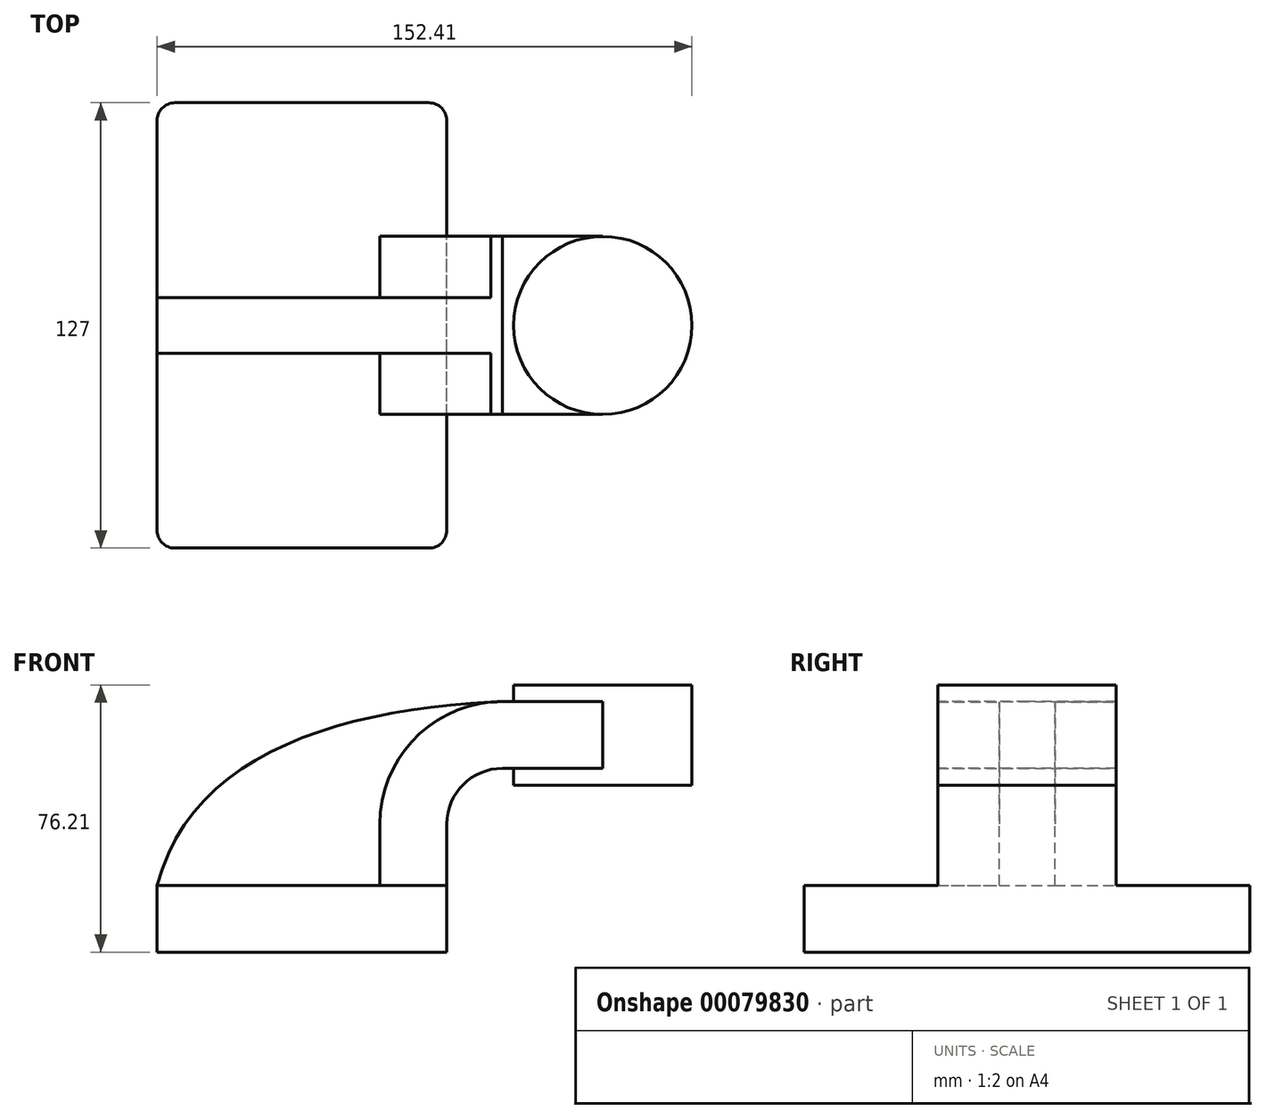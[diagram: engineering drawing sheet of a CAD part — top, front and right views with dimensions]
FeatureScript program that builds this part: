
annotation { "Feature Type Name" : "Feature", "Feature Type Description" : "" }
export const myFeature = defineFeature(function(context is Context, id is Id, definition is map)
    precondition{}
    {
        {
            var Q0;
            Q0=qCreatedBy(makeId("Front.planeOp"),FACE);
            var sketch = newSketch(context, id + "F0", { "sketchPlane" : qUnion([Q0])});
            skLineSegment(sketch, "E0.bottom", {"start": v(-41.28, 9.52) * mm, "end": v(41.28, 9.53) * mm});
            skLineSegment(sketch, "E0.top", {"start": v(-41.28, -9.53) * mm, "end": v(41.28, -9.53) * mm});
            skLineSegment(sketch, "E0.left", {"start": v(-41.28, 9.52) * mm, "end": v(-41.28, -9.53) * mm});
            skLineSegment(sketch, "E0.right", {"start": v(41.28, 9.53) * mm, "end": v(41.28, -9.52) * mm});
            skPoint(sketch, "E0.middle", {"position": v(0, 0) * mm});
            skLineSegment(sketch, "E1.bottom", {"start": v(60.33, 38.1) * mm, "end": v(111.13, 38.1) * mm});
            skLineSegment(sketch, "E1.top", {"start": v(60.32, 66.68) * mm, "end": v(111.12, 66.68) * mm});
            skLineSegment(sketch, "E1.left", {"start": v(60.33, 38.1) * mm, "end": v(60.32, 66.68) * mm});
            skLineSegment(sketch, "E1.right", {"start": v(111.13, 38.1) * mm, "end": v(111.12, 66.68) * mm});
            skPoint(sketch, "E1.middle", {"position": v(85.73, 52.39) * mm});
            skLineSegment(sketch, "E2", {"start": v(41.27, 9.53) * mm, "end": v(41.27, 27) * mm});
            skArc(sketch, "E3", {"start": v(57.15, 42.88) * mm, "mid": v(45.92, 38.23) * mm, "end": v(41.27, 27) * mm});
            skLineSegment(sketch, "E4", {"start": v(57.15, 42.88) * mm, "end": v(85.73, 42.88) * mm});
            skLineSegment(sketch, "E5.0", {"start": v(57.15, 61.93) * mm, "end": v(85.73, 61.93) * mm});
            skArc(sketch, "E5.1", {"start": v(57.15, 61.93) * mm, "mid": v(32.45, 51.7) * mm, "end": v(22.23, 27) * mm});
            skLineSegment(sketch, "E5.2", {"start": v(22.22, 9.53) * mm, "end": v(22.22, 27) * mm});
            skLineSegment(sketch, "E6", {"start": v(85.73, 38.1) * mm, "end": v(85.73, 66.68) * mm});
            skPoint(sketch, "E6.startSnap0", {"position": v(85.73, 38.1) * mm});
            skFitSpline(sketch, "E7", {"points": [v(-41.28, 9.52) * mm, v(57.15, 61.93) * mm], "startDerivative": vector(29.97, 113.63) * mm, "endDerivative": vector(137.51, 5.68) * mm});
            skSolve(sketch);
        }
        {
            var Q0;
            Q0=makeQuery(id+"F0.imprint","IMPRINT",FACE,{"disambiguationData":[TD([[makeQuery(id+"F0.imprint","IMPRINT",EDGE,{"derivedFrom":sQuery(id+"F0.wireOp",EDGE,"E0.top")}),1.0]])]});
            extrude(context, id + "F1", {"entities" : qUnion([Q0]), "endBound" : BoundingType.SYMMETRIC, "depth" : 127 * mm});
        }
        {
            var Q0;
            {var subQ1=sQuery(id+"F0.wireOp",EDGE,"E2");Q0=makeQuery(id+"F0.imprint","IMPRINT",FACE,{"disambiguationData":[TD([[makeQuery(id+"F0.imprint","IMPRINT",EDGE,{"derivedFrom":subQ1}),1.0]])]});}
            var Q1;
            {var subQ0=sQuery(id+"F0.wireOp",EDGE,"E4");var subQ1=sQuery(id+"F0.wireOp",EDGE,"E1.left");var subQ2=makeQuery(id+"F0.imprint","INTERSECT",VERTEX,{"derivedFrom":[subQ1,subQ0]});Q1=makeQuery(id+"F0.imprint","IMPRINT",FACE,{"disambiguationData":[TD([[makeQuery(id+"F0.imprint","IMPRINT",EDGE,{"disambiguationData":[TD([[subQ2,-1.0]])],"derivedFrom":subQ1}),-1.0]])]});}
            extrude(context, id + "F2", {"entities" : qUnion([Q0, Q1]), "operationType" : NewBodyOperationType.ADD, "endBound" : BoundingType.SYMMETRIC, "depth" : 50.8 * mm});
        }
        {
            var Q0;
            {var subQ3=sQuery(id+"F0.wireOp",EDGE,"E5.2");Q0=makeQuery(id+"F0.imprint","IMPRINT",FACE,{"disambiguationData":[TD([[makeQuery(id+"F0.imprint","IMPRINT",EDGE,{"derivedFrom":subQ3}),1.0]])]});}
            extrude(context, id + "F3", {"entities" : qUnion([Q0]), "operationType" : NewBodyOperationType.ADD, "endBound" : BoundingType.SYMMETRIC, "depth" : 15.88 * mm});
        }
        {
            var Q0;
            {var subQ0=sQuery(id+"F0.wireOp",EDGE,"E1.right");Q0=makeQuery(id+"F0.imprint","IMPRINT",FACE,{"disambiguationData":[TD([[makeQuery(id+"F0.imprint","IMPRINT",EDGE,{"derivedFrom":subQ0}),1.0]])]});}
            var Q1;
            Q1=sQuery(id+"F0.wireOp",EDGE,"E6");
            revolve(context, id + "F4", {"operationType" : NewBodyOperationType.ADD, "entities" : qUnion([Q0]), "axis" : qUnion([Q1]), "revolveType" : RevolveType.FULL});
        }
        {
            var Q0;
            Q0=makeQuery(id+"F1.opExtrude","CAP_EDGE",EDGE,{"disambiguationData":[OSD([sQuery(id+"F0.wireOp",EDGE,"E0.right")])],"isStart":false});
            var Q1;
            Q1=makeQuery(id+"F1.opExtrude","CAP_EDGE",EDGE,{"disambiguationData":[OSD([sQuery(id+"F0.wireOp",EDGE,"E0.left")])],"isStart":false});
            var Q2;
            Q2=makeQuery(id+"F1.opExtrude","CAP_EDGE",EDGE,{"disambiguationData":[OSD([sQuery(id+"F0.wireOp",EDGE,"E0.right")])],"isStart":true});
            var Q3;
            Q3=makeQuery(id+"F1.opExtrude","CAP_EDGE",EDGE,{"disambiguationData":[OSD([sQuery(id+"F0.wireOp",EDGE,"E0.left")])],"isStart":true});
            fillet(context, id + "F5", {"entities" : qUnion([Q0, Q1, Q2, Q3]), "radius" : 5.08 * mm, "tangentPropagation" : true, "allowEdgeOverflow" : false});
        }
    });
